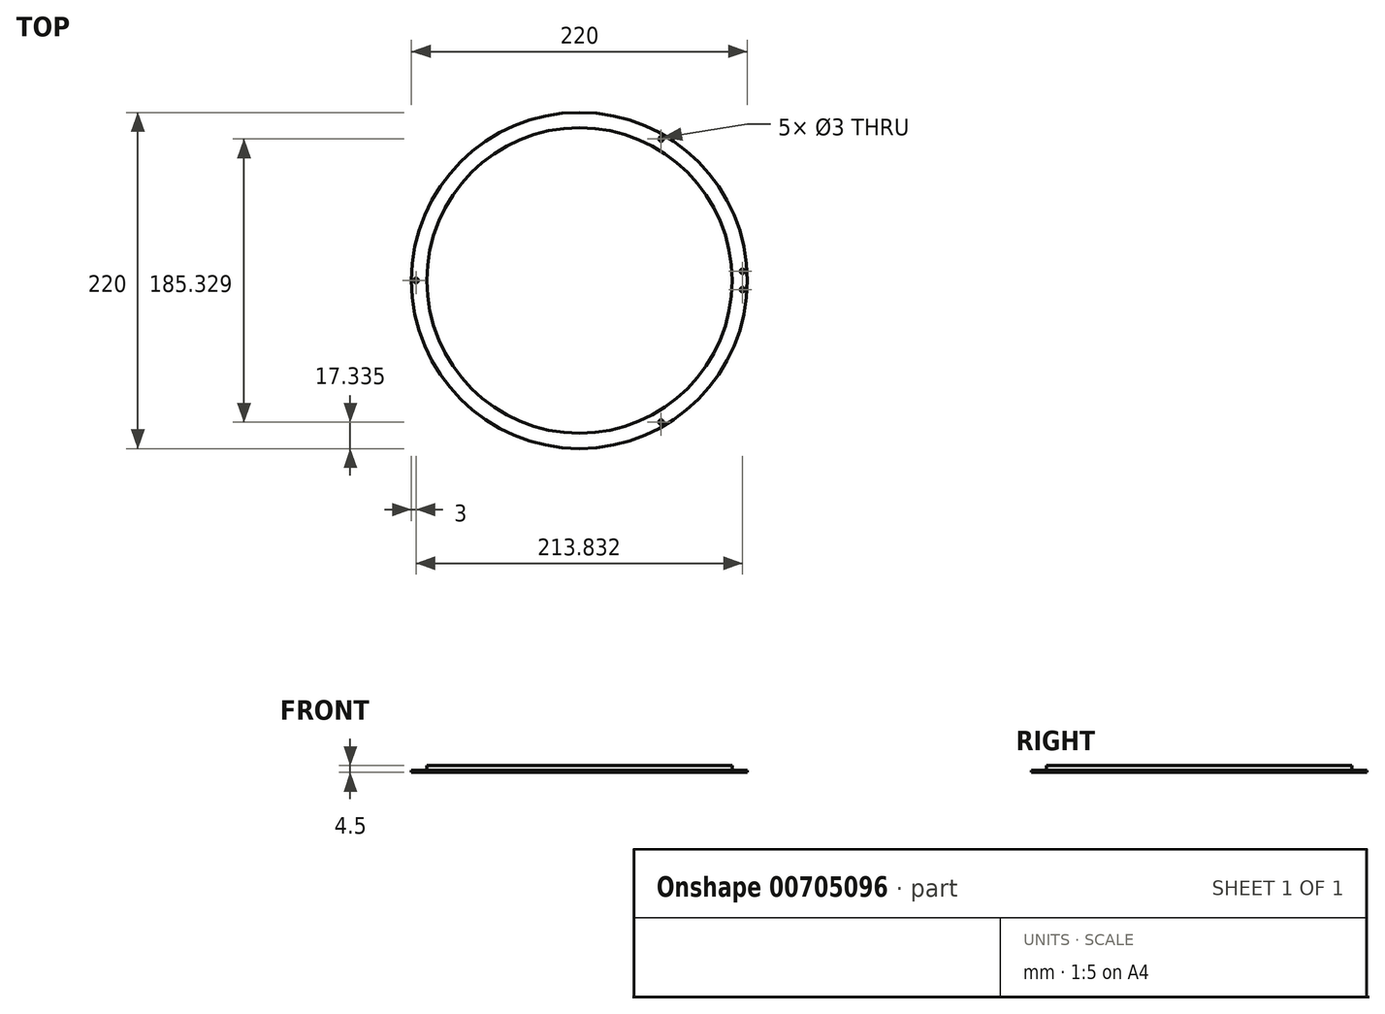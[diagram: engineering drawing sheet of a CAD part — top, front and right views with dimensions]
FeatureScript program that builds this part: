
annotation { "Feature Type Name" : "Feature", "Feature Type Description" : "" }
export const myFeature = defineFeature(function(context is Context, id is Id, definition is map)
    precondition{}
    {
        {
            var Q0;
            Q0=qCreatedBy(makeId("Top.planeOp"),FACE);
            var sketch = newSketch(context, id + "F0", { "sketchPlane" : qUnion([Q0])});
            skCircle(sketch, "E0", {"center": v(0, 0) * mm, "radius": 110 * mm});
            skPoint(sketch, "E1", {"position": v(-107, 0) * mm});
            skPoint(sketch, "E2", {"position": v(53.5, 92.66) * mm});
            skPoint(sketch, "E3", {"position": v(53.5, -92.66) * mm});
            skLineSegment(sketch, "E4", {"start": v(0, 0) * mm, "end": v(-107, 0) * mm, "construction": true});
            skLineSegment(sketch, "E5", {"start": v(0, 0) * mm, "end": v(53.5, 92.66) * mm, "construction": true});
            skLineSegment(sketch, "E6", {"start": v(0, 0) * mm, "end": v(53.5, -92.66) * mm, "construction": true});
            skPoint(sketch, "E7", {"position": v(106.83, 6) * mm});
            skPoint(sketch, "E8", {"position": v(106.83, -6) * mm});
            skLineSegment(sketch, "E9", {"start": v(0, 0) * mm, "end": v(106.83, 6) * mm, "construction": true});
            skSolve(sketch);
        }
        {
            var Q0;
            Q0=makeQuery(id+"F0.imprint","IMPRINT",FACE,{"disambiguationData":[TD([[makeQuery(id+"F0.imprint","IMPRINT",EDGE,{"derivedFrom":sQuery(id+"F0.wireOp",EDGE,"E0")}),1.0]])]});
            extrude(context, id + "F1", {"entities" : qUnion([Q0]), "depth" : 1.5 * mm, "offsetDistance" : 25 * mm});
        }
        {
            var Q0;
            Q0=sQuery(id+"F0.wireOp",VERTEX,"E1");
            var Q1;
            Q1=sQuery(id+"F0.wireOp",VERTEX,"E2");
            var Q2;
            Q2=sQuery(id+"F0.wireOp",VERTEX,"E3");
            var Q3;
            Q3=sQuery(id+"F0.wireOp",VERTEX,"E7");
            var Q4;
            Q4=sQuery(id+"F0.wireOp",VERTEX,"E8");
            var Q5;
            Q5=makeQuery(id+"F1.opExtrude","SWEPT_BODY",BODY,{"disambiguationData":[OSD([sQuery(id+"F0.wireOp",EDGE,"E0")])]});
            hole(context, id + "F2", {"style" : HoleStyle.SIMPLE, "endStyle" : HoleEndStyle.BLIND, "oppositeDirection" : true, "holeDiameter" : 3 * mm, "majorDiameter" : 5 * mm, "holeDepth" : 10 * mm, "isTappedThrough" : true, "tappedDepth" : 15 * mm, "tapClearance" : 0, "startFromSketch" : true, "locations" : qUnion([Q0, Q1, Q2, Q3, Q4]), "scope" : qUnion([Q5])});
        }
        {
            var Q0;
            Q0=makeQuery(id+"F1.opExtrude","CAP_FACE",FACE,{"disambiguationData":[OSD([sQuery(id+"F0.wireOp",EDGE,"E0")])],"isStart":false});
            var sketch = newSketch(context, id + "F3", { "sketchPlane" : qUnion([Q0])});
            skCircle(sketch, "E10", {"center": v(0, 0) * mm, "radius": 100 * mm});
            skSolve(sketch);
        }
        {
            var Q0;
            Q0=makeQuery(id+"F3.imprint","IMPRINT",FACE,{"disambiguationData":[TD([[makeQuery(id+"F3.imprint","IMPRINT",EDGE,{"derivedFrom":sQuery(id+"F3.wireOp",EDGE,"E10")}),1.0]])]});
            extrude(context, id + "F4", {"entities" : qUnion([Q0]), "depth" : 3 * mm, "offsetDistance" : 25 * mm});
        }
    });
